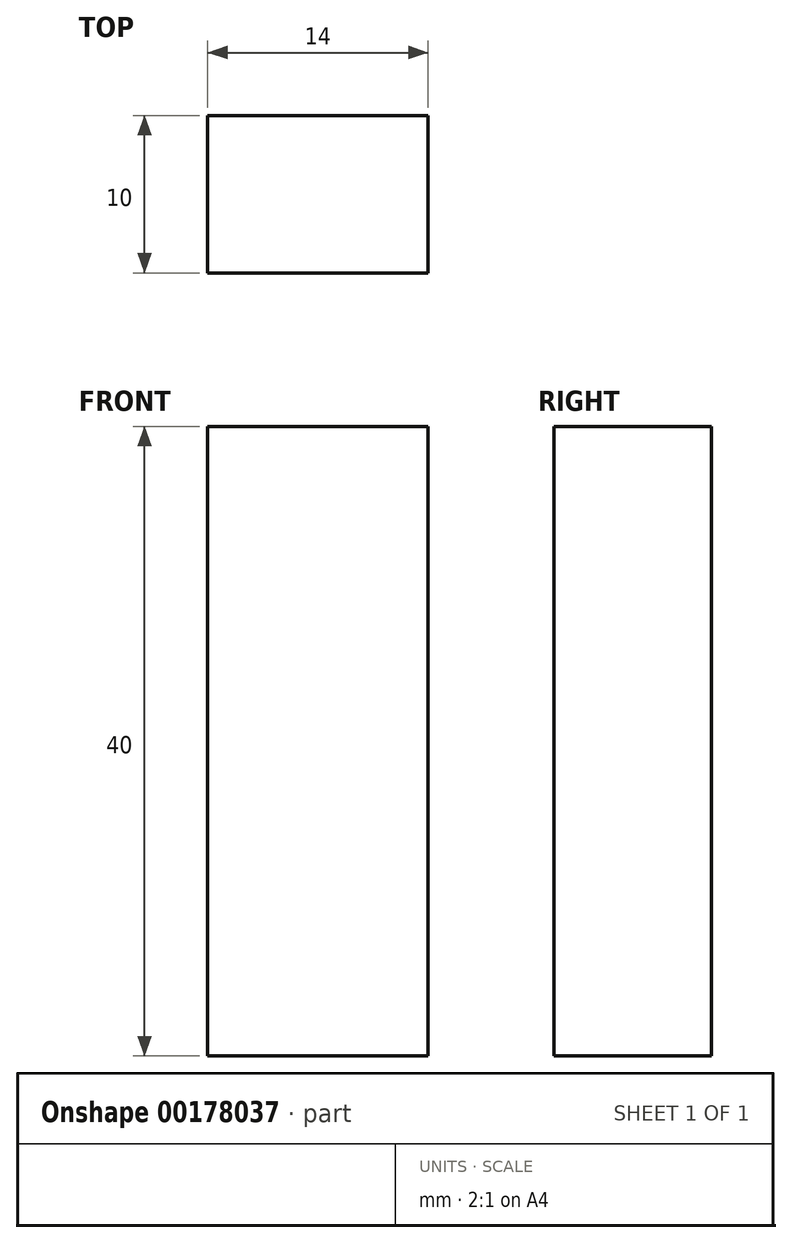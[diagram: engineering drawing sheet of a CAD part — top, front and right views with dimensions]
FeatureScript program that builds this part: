
annotation { "Feature Type Name" : "Feature", "Feature Type Description" : "" }
export const myFeature = defineFeature(function(context is Context, id is Id, definition is map)
    precondition{}
    {
        {
            var Q0;
            Q0=qCreatedBy(makeId("Right.planeOp"),FACE);
            var sketch = newSketch(context, id + "F0", { "sketchPlane" : qUnion([Q0])});
            skLineSegment(sketch, "E0.bottom", {"start": v(5, -20) * mm, "end": v(-5, -20) * mm});
            skLineSegment(sketch, "E0.top", {"start": v(5, 20) * mm, "end": v(-5, 20) * mm});
            skLineSegment(sketch, "E0.left", {"start": v(5, -20) * mm, "end": v(5, 20) * mm});
            skLineSegment(sketch, "E0.right", {"start": v(-5, -20) * mm, "end": v(-5, 20) * mm});
            skPoint(sketch, "E0.middle", {"position": v(0, 0) * mm});
            skSolve(sketch);
        }
        {
            var Q0;
            Q0=makeQuery(id+"F0.imprint","IMPRINT",FACE,{"disambiguationData":[TD([[makeQuery(id+"F0.imprint","IMPRINT",EDGE,{"derivedFrom":sQuery(id+"F0.wireOp",EDGE,"E0.bottom")}),-1.0]])]});
            extrude(context, id + "F1", {"entities" : qUnion([Q0]), "depth" : 7 * mm, "hasSecondDirection" : true, "secondDirectionOppositeDirection" : true, "secondDirectionDepth" : 7 * mm});
        }
    });
